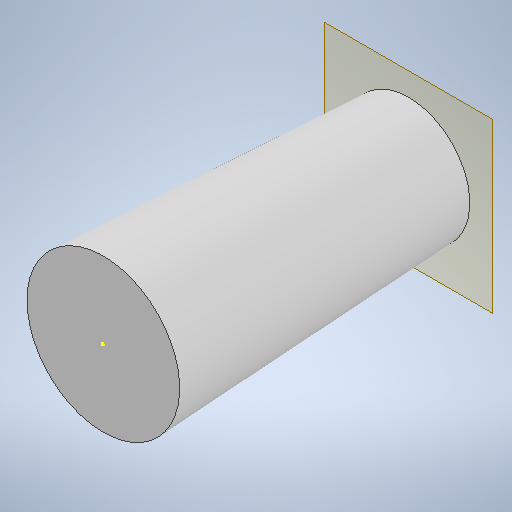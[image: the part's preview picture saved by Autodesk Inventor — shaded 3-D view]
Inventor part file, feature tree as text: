
AUTODESK INVENTOR PART (.ipt)
format: ipt  version: 2025.2 (Build 292293000, 293)  size: 216,064 bytes
history: native  units: mm
features: sketch x3, plane x1, loft x1
ambient origin geometry x8: Origin, YZ Plane, XZ Plane, XY Plane, X Axis, Y Axis, Z Axis, Center Point
bodies: Solid1 (feature_tree)
feature tree (5):
  sketch  "Sketch1"  dims[d0=50.0mm d1=-100.0mm]
  plane  "Work Plane1"
  sketch  "Sketch2"  dims[d3=40.0mm]
  loft  "Loft1"
  sketch  "Sketch3"  dims[d4=0.0mm d5=90.0deg d6=0.0mm d7=90.0deg]
